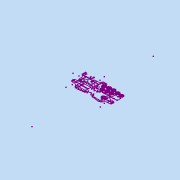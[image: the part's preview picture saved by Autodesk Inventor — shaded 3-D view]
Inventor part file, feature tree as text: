
AUTODESK INVENTOR PART (.ipt)
format: ipt  version: 2015 (Build 190159000, 159)  size: 289,280 bytes
history: native  units: in
note: dims shown in document units (in); Inventor stores cm internally (conversion verified against a paired STEP export)
features: sketch x1
ambient origin geometry x8: Origin, YZ Plane, XZ Plane, XY Plane, X Axis, Y Axis, Z Axis, Center Point
feature tree (1):
  sketch  "Sketch1"
